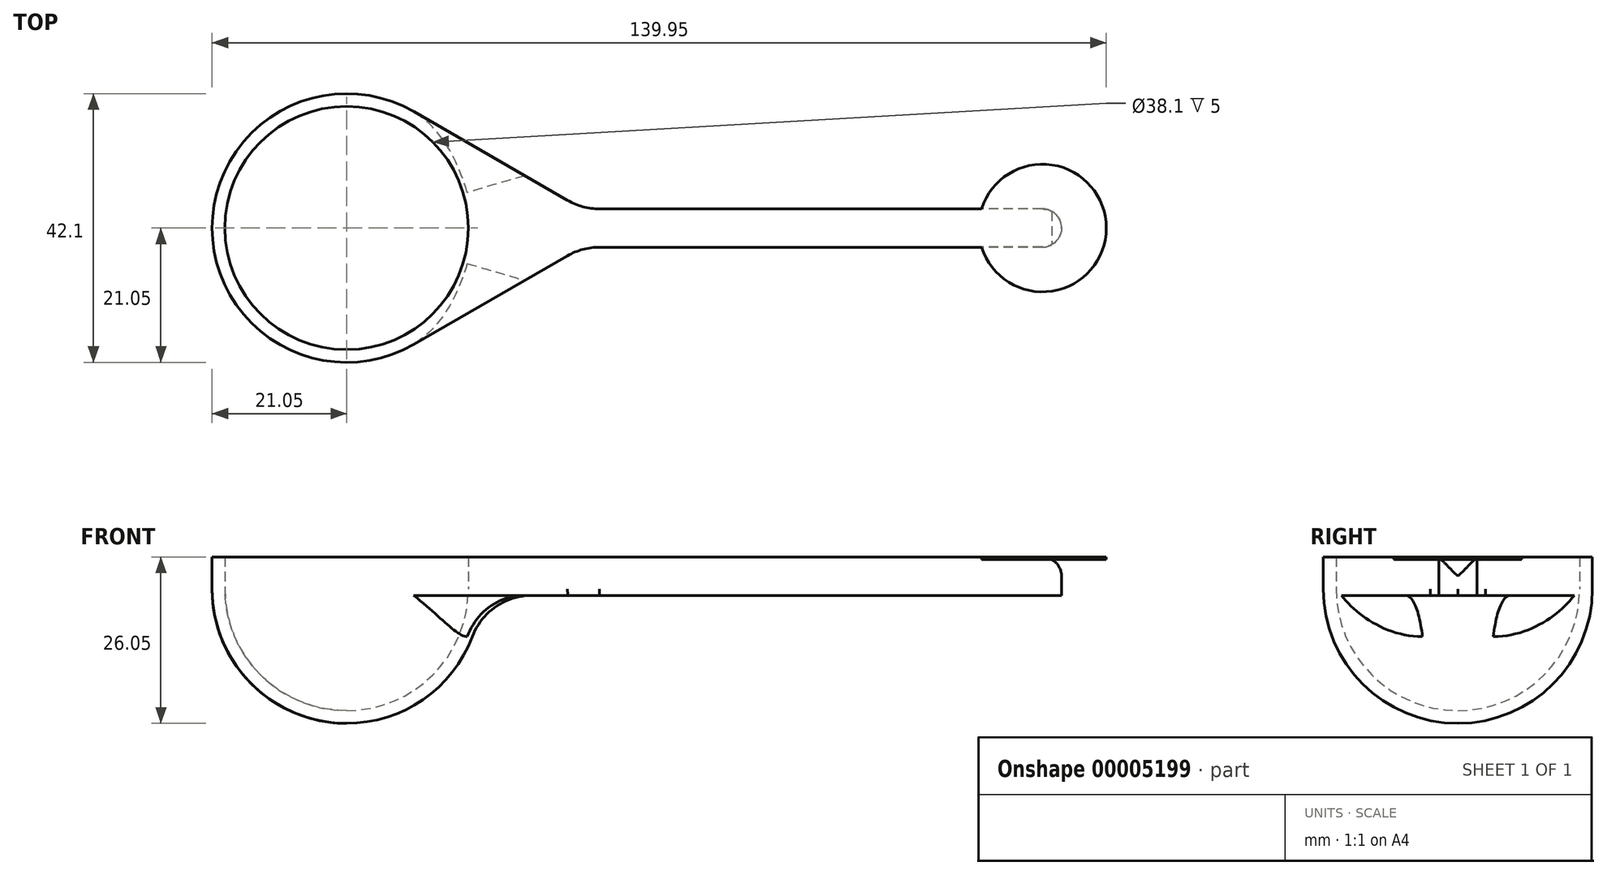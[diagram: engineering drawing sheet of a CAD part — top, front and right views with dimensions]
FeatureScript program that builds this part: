
annotation { "Feature Type Name" : "Feature", "Feature Type Description" : "" }
export const myFeature = defineFeature(function(context is Context, id is Id, definition is map)
    precondition{}
    {
        {
            var Q0;
            Q0=qCreatedBy(makeId("Front.planeOp"),FACE);
            var sketch = newSketch(context, id + "F0", { "sketchPlane" : qUnion([Q0])});
            skCircle(sketch, "E0", {"center": v(0, 0) * mm, "radius": 19.05 * mm, "construction": true});
            skCircle(sketch, "E1", {"center": v(0, 0) * mm, "radius": 21.05 * mm, "construction": true});
            skLineSegment(sketch, "E2", {"start": v(0, 0) * mm, "end": v(0, 19.05) * mm, "construction": true});
            skArc(sketch, "E3", {"start": v(-19.05, 0) * mm, "mid": v(-13.47, -13.47) * mm, "end": v(0, -19.05) * mm});
            skArc(sketch, "E4", {"start": v(-21.05, 0) * mm, "mid": v(-14.88, -14.88) * mm, "end": v(0, -21.05) * mm});
            skLineSegment(sketch, "E5", {"start": v(-21.05, 0) * mm, "end": v(-19.05, 0) * mm});
            skLineSegment(sketch, "E6", {"start": v(0, -19.05) * mm, "end": v(0, -21.05) * mm});
            skSolve(sketch);
        }
        {
            var Q0;
            Q0=qSketchRegion(id+"F0",true);
            var Q1;
            Q1=sQuery(id+"F0.wireOp",EDGE,"E6");
            revolve(context, id + "F1", {"entities" : qUnion([Q0]), "axis" : qUnion([Q1]), "revolveType" : RevolveType.FULL});
        }
        {
            var Q0;
            Q0=makeQuery(id+"F1.opRevolve","SWEPT_FACE",FACE,{"disambiguationData":[OSD([sQuery(id+"F0.wireOp",EDGE,"E5")])]});
            var sketch = newSketch(context, id + "F2", { "sketchPlane" : qUnion([Q0])});
            skLineSegment(sketch, "E7", {"start": v(0, 0) * mm, "end": v(19.05, 0) * mm, "construction": true});
            skArc(sketch, "E8.0", {"start": v(9.52, -16.5) * mm, "mid": v(19.05, 0) * mm, "end": v(9.52, 16.5) * mm});
            skLineSegment(sketch, "E9", {"start": v(0, 0) * mm, "end": v(9.53, 16.5) * mm, "construction": true});
            skLineSegment(sketch, "E10", {"start": v(9.53, 16.5) * mm, "end": v(10.53, 18.23) * mm});
            skLineSegment(sketch, "E11.MirrorCS", {"start": v(9.53, -16.5) * mm, "end": v(10.53, -18.23) * mm});
            skLineSegment(sketch, "E12", {"start": v(10.52, 18.23) * mm, "end": v(36.9, 3) * mm});
            skLineSegment(sketch, "E13.MirrorCS", {"start": v(10.53, -18.23) * mm, "end": v(36.9, -3) * mm});
            skLineSegment(sketch, "E14", {"start": v(36.9, 3) * mm, "end": v(36.9, -3) * mm});
            skSolve(sketch);
        }
        {
            var Q0;
            Q0 = qSketchRegion(id + "F2", true);
            extrude(context, id + "F3", {"entities" : qUnion([Q0]), "operationType" : NewBodyOperationType.ADD, "oppositeDirection" : true, "depth" : 1 * mm});
        }
        {
            var Q0;
            Q0=makeQuery(id+"F3.opExtrude","SWEPT_FACE",FACE,{"disambiguationData":[OSD([sQuery(id+"F2.wireOp",EDGE,"E10")])]});
            extrude(context, id + "F4", {"entities" : qUnion([Q0]), "operationType" : NewBodyOperationType.REMOVE, "endBound" : BoundingType.THROUGH_ALL, "oppositeDirection" : true, "depth" : 25 * mm});
        }
        {
            var Q0;
            Q0=makeQuery(id+"F3.opExtrude","SWEPT_FACE",FACE,{"disambiguationData":[OSD([sQuery(id+"F2.wireOp",EDGE,"E11.MirrorCS")])]});
            extrude(context, id + "F5", {"entities" : qUnion([Q0]), "operationType" : NewBodyOperationType.REMOVE, "endBound" : BoundingType.THROUGH_ALL, "oppositeDirection" : true, "depth" : 25 * mm});
        }
        {
            var Q0;
            Q0=makeQuery(id+"F3.opExtrude","SWEPT_FACE",FACE,{"disambiguationData":[OSD([sQuery(id+"F2.wireOp",EDGE,"E14")])]});
            extrude(context, id + "F6", {"entities" : qUnion([Q0]), "operationType" : NewBodyOperationType.ADD, "depth" : 75 * mm});
        }
        {
            var Q0;
            Q0=makeQuery(id+"F3.boolean.opBoolean","INTERSECT",EDGE,{"derivedFrom":[makeQuery(id+"F1.opRevolve","SWEPT_FACE",FACE,{"disambiguationData":[OSD([sQuery(id+"F0.wireOp",EDGE,"E4")])]}),makeQuery(id+"F3.opExtrude","CAP_FACE",FACE,{"disambiguationData":[OSD([sQuery(id+"F2.wireOp",EDGE,"E8.0"),sQuery(id+"F2.wireOp",EDGE,"E10"),sQuery(id+"F2.wireOp",EDGE,"E11.MirrorCS"),sQuery(id+"F2.wireOp",EDGE,"E12"),sQuery(id+"F2.wireOp",EDGE,"E13.MirrorCS"),sQuery(id+"F2.wireOp",EDGE,"E14")])],"isStart":false})]});
            var Q1;
            {var subQ0=sQuery(id+"F2.wireOp",EDGE,"E14");var subQ1=sQuery(id+"F2.wireOp",EDGE,"E11.MirrorCS");var subQ2=sQuery(id+"F0.wireOp",EDGE,"E4");Q1=makeQuery(id+"F6.boolean.opBoolean","MERGE",EDGE,{"derivedFrom":[makeQuery(id+"F5.boolean.opBoolean","INTERSECT",EDGE,{"derivedFrom":[makeQuery(id+"F3.opExtrude","SWEPT_FACE",FACE,{"disambiguationData":[OSD([subQ0])]}),makeQuery(id+"F5.opExtrude","SWEPT_FACE",FACE,{"disambiguationData":[OSD([subQ2,subQ1])]})]}),makeQuery(id+"F6.opExtrude","CAP_EDGE",EDGE,{"disambiguationData":[OSD([subQ2,subQ1,subQ0])],"isStart":true})]});}
            var Q2;
            {var subQ0=sQuery(id+"F2.wireOp",EDGE,"E14");var subQ1=sQuery(id+"F2.wireOp",EDGE,"E10");var subQ2=sQuery(id+"F0.wireOp",EDGE,"E4");Q2=makeQuery(id+"F6.boolean.opBoolean","MERGE",EDGE,{"derivedFrom":[makeQuery(id+"F4.boolean.opBoolean","INTERSECT",EDGE,{"derivedFrom":[makeQuery(id+"F3.opExtrude","SWEPT_FACE",FACE,{"disambiguationData":[OSD([subQ0])]}),makeQuery(id+"F4.opExtrude","SWEPT_FACE",FACE,{"disambiguationData":[OSD([subQ2,subQ1])]})]}),makeQuery(id+"F6.opExtrude","CAP_EDGE",EDGE,{"disambiguationData":[OSD([subQ2,subQ1,subQ0])],"isStart":true})]});}
            fillet(context, id + "F7", {"entities" : qUnion([Q0, Q1, Q2]), "radius" : 10 * mm, "tangentPropagation" : true, "allowEdgeOverflow" : false});
        }
        {
            var Q0;
            {var subQ0=sQuery(id+"F2.wireOp",EDGE,"E14");Q0=makeQuery(id+"F6.boolean.opBoolean","MERGE",FACE,{"derivedFrom":[makeQuery(id+"F3.boolean.opBoolean","MERGE",FACE,{"derivedFrom":[makeQuery(id+"F1.opRevolve","SWEPT_FACE",FACE,{"disambiguationData":[OSD([sQuery(id+"F0.wireOp",EDGE,"E5")])]}),makeQuery(id+"F3.opExtrude","CAP_FACE",FACE,{"disambiguationData":[OSD([sQuery(id+"F2.wireOp",EDGE,"E8.0"),sQuery(id+"F2.wireOp",EDGE,"E10"),sQuery(id+"F2.wireOp",EDGE,"E11.MirrorCS"),sQuery(id+"F2.wireOp",EDGE,"E12"),sQuery(id+"F2.wireOp",EDGE,"E13.MirrorCS"),subQ0])],"isStart":true})]}),makeQuery(id+"F6.opExtrude","SWEPT_FACE",FACE,{"disambiguationData":[OSD([subQ0]),TDD([makeQuery(id+"F3.opExtrude","CAP_EDGE",EDGE,{"disambiguationData":[OSD([subQ0])],"isStart":true})])]})]});}
            extrude(context, id + "F8", {"entities" : qUnion([Q0]), "operationType" : NewBodyOperationType.ADD, "depth" : 5 * mm});
        }
        {
            var Q0;
            Q0=makeQuery(id+"F8.opExtrude","CAP_EDGE",EDGE,{"disambiguationData":[OSD([sQuery(id+"F2.wireOp",EDGE,"E14")])],"isStart":false});
            var Q1;
            Q1=makeQuery(id+"F8.opExtrude","SWEPT_EDGE",EDGE,{"disambiguationData":[OSD([sQuery(id+"F2.wireOp",EDGE,"E13.MirrorCS"),sQuery(id+"F2.wireOp",EDGE,"E14")])]});
            var Q2;
            Q2=makeQuery(id+"F8.opExtrude","SWEPT_EDGE",EDGE,{"disambiguationData":[OSD([sQuery(id+"F2.wireOp",EDGE,"E12"),sQuery(id+"F2.wireOp",EDGE,"E14")])]});
            fillet(context, id + "F9", {"entities" : qUnion([Q0, Q1, Q2]), "radius" : 3 * mm, "tangentPropagation" : true, "allowEdgeOverflow" : false});
        }
        {
            var Q0;
            Q0=makeQuery(id+"F8.opExtrude","CAP_FACE",FACE,{"disambiguationData":[OSD([sQuery(id+"F0.wireOp",EDGE,"E5"),sQuery(id+"F2.wireOp",EDGE,"E8.0"),sQuery(id+"F2.wireOp",EDGE,"E10"),sQuery(id+"F2.wireOp",EDGE,"E11.MirrorCS"),sQuery(id+"F2.wireOp",EDGE,"E12"),sQuery(id+"F2.wireOp",EDGE,"E13.MirrorCS"),sQuery(id+"F2.wireOp",EDGE,"E14")])],"isStart":false});
            var sketch = newSketch(context, id + "F10", { "sketchPlane" : qUnion([Q0])});
            skCircle(sketch, "E15", {"center": v(108.9, 0) * mm, "radius": 10 * mm});
            skSolve(sketch);
        }
        {
            var Q0;
            Q0 = qSketchRegion(id + "F10", true);
            extrude(context, id + "F11", {"entities" : qUnion([Q0]), "operationType" : NewBodyOperationType.ADD, "oppositeDirection" : true, "depth" : 0.4 * mm});
        }
    });
